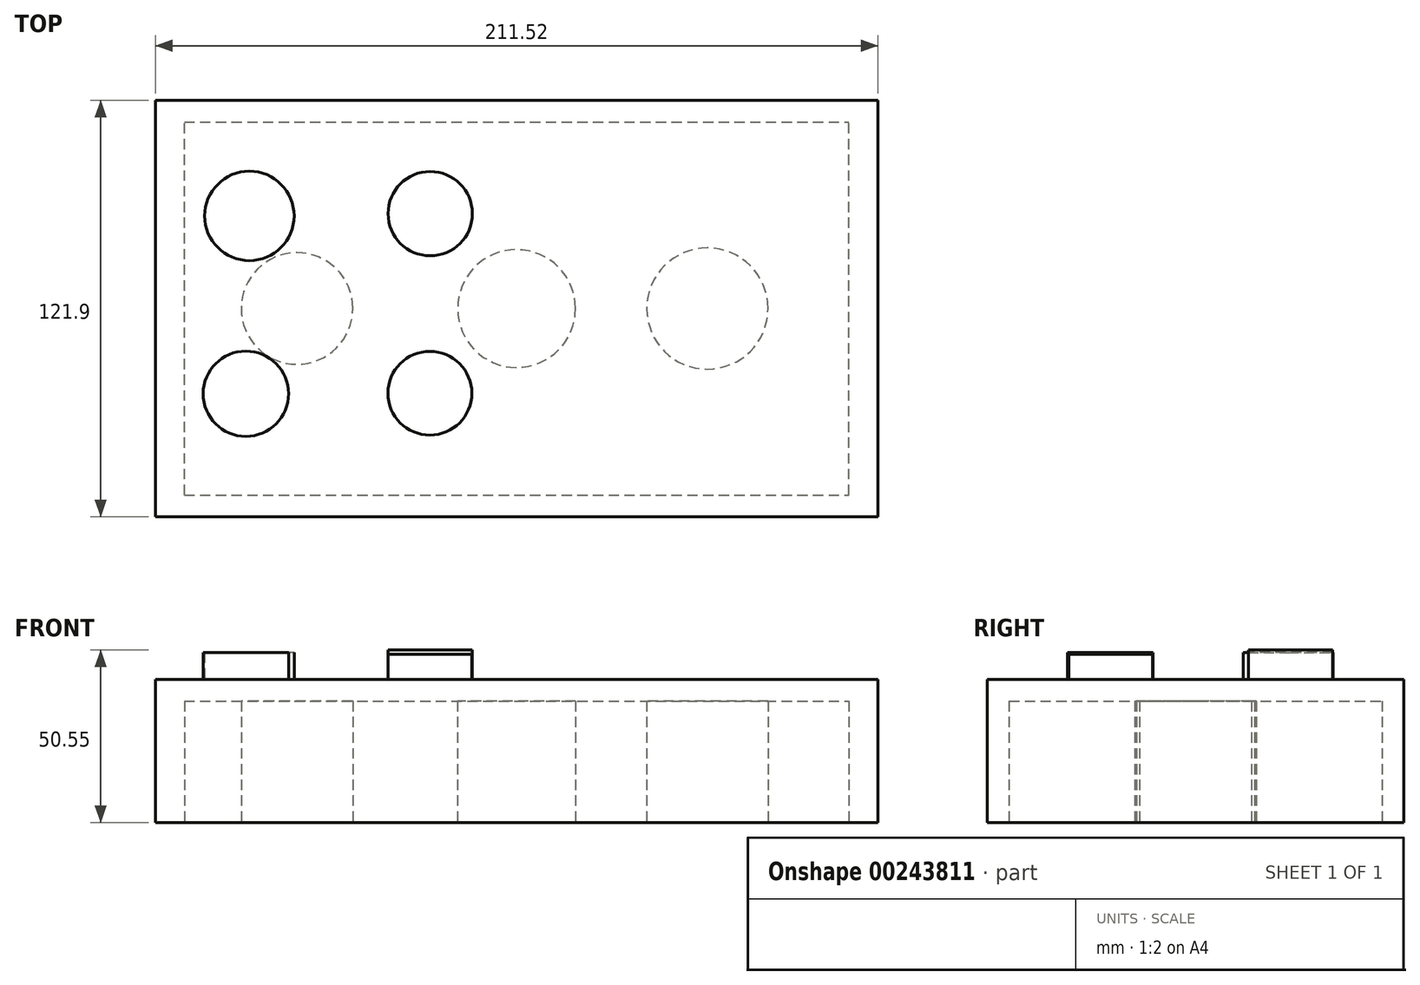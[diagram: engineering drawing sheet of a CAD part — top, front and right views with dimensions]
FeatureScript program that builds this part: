
annotation { "Feature Type Name" : "Feature", "Feature Type Description" : "" }
export const myFeature = defineFeature(function(context is Context, id is Id, definition is map)
    precondition{}
    {
        {
            var Q0;
            Q0=qCreatedBy(makeId("Top.planeOp"),FACE);
            var sketch = newSketch(context, id + "F0", { "sketchPlane" : qUnion([Q0])});
            skLineSegment(sketch, "E0.bottom", {"start": v(-105.76, 60.95) * mm, "end": v(105.76, 60.95) * mm});
            skLineSegment(sketch, "E0.top", {"start": v(-105.76, -60.95) * mm, "end": v(105.76, -60.95) * mm});
            skLineSegment(sketch, "E0.left", {"start": v(-105.76, 60.95) * mm, "end": v(-105.76, -60.95) * mm});
            skLineSegment(sketch, "E0.right", {"start": v(105.76, 60.95) * mm, "end": v(105.76, -60.95) * mm});
            skPoint(sketch, "E0.middle", {"position": v(0, 0) * mm});
            skSolve(sketch);
        }
        {
            var Q0;
            Q0 = qSketchRegion(id + "F0", true);
            extrude(context, id + "F1", {"entities" : qUnion([Q0]), "depth" : 41.9 * mm});
        }
        {
            var Q0;
            Q0=makeQuery(id+"F1.opExtrude","CAP_FACE",FACE,{"disambiguationData":[OSD([sQuery(id+"F0.wireOp",EDGE,"E0.bottom"),sQuery(id+"F0.wireOp",EDGE,"E0.top"),sQuery(id+"F0.wireOp",EDGE,"E0.left"),sQuery(id+"F0.wireOp",EDGE,"E0.right")])],"isStart":false});
            var sketch = newSketch(context, id + "F2", { "sketchPlane" : qUnion([Q0])});
            skCircle(sketch, "E1", {"center": v(-78.22, 27.11) * mm, "radius": 13.1 * mm});
            skSolve(sketch);
        }
        {
            var Q0;
            Q0=makeQuery(id+"F2.imprint","IMPRINT",FACE,{"disambiguationData":[TD([[makeQuery(id+"F2.imprint","IMPRINT",EDGE,{"derivedFrom":sQuery(id+"F2.wireOp",EDGE,"E1")}),1.0]])]});
            extrude(context, id + "F3", {"entities" : qUnion([Q0]), "operationType" : NewBodyOperationType.ADD, "depth" : 7.87 * mm});
        }
        {
            var Q0;
            Q0=makeQuery(id+"F2.imprint","IMPRINT",FACE,{"disambiguationData":[TD([[makeQuery(id+"F2.imprint","IMPRINT",EDGE,{"derivedFrom":sQuery(id+"F2.wireOp",EDGE,"E1")}),-1.0]])]});
            var sketch = newSketch(context, id + "F4", { "sketchPlane" : qUnion([Q0])});
            skCircle(sketch, "E2", {"center": v(-79.26, -24.95) * mm, "radius": 12.5 * mm});
            skSolve(sketch);
        }
        {
            var Q0;
            Q0 = qSketchRegion(id + "F4", true);
            extrude(context, id + "F5", {"entities" : qUnion([Q0]), "operationType" : NewBodyOperationType.ADD, "depth" : 7.87 * mm});
        }
        {
            var Q0;
            Q0=makeQuery(id+"F2.imprint","IMPRINT",FACE,{"disambiguationData":[TD([[makeQuery(id+"F2.imprint","IMPRINT",EDGE,{"derivedFrom":sQuery(id+"F2.wireOp",EDGE,"E1")}),-1.0]])]});
            var sketch = newSketch(context, id + "F6", { "sketchPlane" : qUnion([Q0])});
            skCircle(sketch, "E3", {"center": v(-25.29, 27.78) * mm, "radius": 12.34 * mm});
            skSolve(sketch);
        }
        {
            var Q0;
            Q0 = qSketchRegion(id + "F6", true);
            extrude(context, id + "F7", {"entities" : qUnion([Q0]), "operationType" : NewBodyOperationType.ADD, "depth" : 8.64 * mm});
        }
        {
            var Q0;
            Q0=makeQuery(id+"F2.imprint","IMPRINT",FACE,{"disambiguationData":[TD([[makeQuery(id+"F2.imprint","IMPRINT",EDGE,{"derivedFrom":sQuery(id+"F2.wireOp",EDGE,"E1")}),-1.0]])]});
            var sketch = newSketch(context, id + "F8", { "sketchPlane" : qUnion([Q0])});
            skCircle(sketch, "E4", {"center": v(-25.38, -24.8) * mm, "radius": 12.27 * mm});
            skSolve(sketch);
        }
        {
            var Q0;
            Q0 = qSketchRegion(id + "F8", true);
            extrude(context, id + "F9", {"entities" : qUnion([Q0]), "operationType" : NewBodyOperationType.ADD, "depth" : 7.37 * mm});
        }
        {
            var Q0;
            Q0=makeQuery(id+"F0.imprint","IMPRINT",FACE,{"disambiguationData":[TD([[makeQuery(id+"F0.imprint","IMPRINT",EDGE,{"derivedFrom":sQuery(id+"F0.wireOp",EDGE,"E0.bottom")}),-1.0]])]});
            var sketch = newSketch(context, id + "F10", { "sketchPlane" : qUnion([Q0])});
            skLineSegment(sketch, "E5.bottom", {"start": v(-97.25, -54.56) * mm, "end": v(97.25, -54.56) * mm});
            skLineSegment(sketch, "E5.top", {"start": v(-97.25, 54.56) * mm, "end": v(97.25, 54.56) * mm});
            skLineSegment(sketch, "E5.left", {"start": v(-97.25, -54.56) * mm, "end": v(-97.25, 54.56) * mm});
            skLineSegment(sketch, "E5.right", {"start": v(97.25, -54.56) * mm, "end": v(97.25, 54.56) * mm});
            skPoint(sketch, "E5.middle", {"position": v(0, 0) * mm});
            skSolve(sketch);
        }
        {
            var Q0;
            Q0 = qSketchRegion(id + "F10", true);
            extrude(context, id + "F11", {"entities" : qUnion([Q0]), "operationType" : NewBodyOperationType.REMOVE, "depth" : 35.56 * mm});
        }
        {
            var Q0;
            Q0=makeQuery(id+"F0.imprint","IMPRINT",FACE,{"disambiguationData":[TD([[makeQuery(id+"F0.imprint","IMPRINT",EDGE,{"derivedFrom":sQuery(id+"F0.wireOp",EDGE,"E0.bottom")}),-1.0]])]});
            var sketch = newSketch(context, id + "F12", { "sketchPlane" : qUnion([Q0])});
            skCircle(sketch, "E6", {"center": v(0, 0) * mm, "radius": 17.25 * mm});
            skSolve(sketch);
        }
        {
            var Q0;
            Q0=makeQuery(id+"F12.imprint","IMPRINT",FACE,{"disambiguationData":[TD([[makeQuery(id+"F12.imprint","IMPRINT",EDGE,{"derivedFrom":sQuery(id+"F12.wireOp",EDGE,"E6")}),1.0]])]});
            extrude(context, id + "F13", {"entities" : qUnion([Q0]), "operationType" : NewBodyOperationType.ADD, "depth" : 40.85 * mm});
        }
        {
            var Q0;
            Q0=makeQuery(id+"F0.imprint","IMPRINT",FACE,{"disambiguationData":[TD([[makeQuery(id+"F0.imprint","IMPRINT",EDGE,{"derivedFrom":sQuery(id+"F0.wireOp",EDGE,"E0.bottom")}),-1.0]])]});
            var sketch = newSketch(context, id + "F14", { "sketchPlane" : qUnion([Q0])});
            skCircle(sketch, "E7", {"center": v(-64.27, 0) * mm, "radius": 16.34 * mm});
            skSolve(sketch);
        }
        {
            var Q0;
            Q0=makeQuery(id+"F14.imprint","IMPRINT",FACE,{"disambiguationData":[TD([[makeQuery(id+"F14.imprint","IMPRINT",EDGE,{"derivedFrom":sQuery(id+"F14.wireOp",EDGE,"E7")}),1.0]])]});
            extrude(context, id + "F15", {"entities" : qUnion([Q0]), "operationType" : NewBodyOperationType.ADD, "depth" : 40.94 * mm});
        }
        {
            var Q0;
            Q0=makeQuery(id+"F0.imprint","IMPRINT",FACE,{"disambiguationData":[TD([[makeQuery(id+"F0.imprint","IMPRINT",EDGE,{"derivedFrom":sQuery(id+"F0.wireOp",EDGE,"E0.bottom")}),-1.0]])]});
            var sketch = newSketch(context, id + "F16", { "sketchPlane" : qUnion([Q0])});
            skCircle(sketch, "E8", {"center": v(55.83, 0) * mm, "radius": 17.74 * mm});
            skSolve(sketch);
        }
        {
            var Q0;
            Q0=makeQuery(id+"F16.imprint","IMPRINT",FACE,{"disambiguationData":[TD([[makeQuery(id+"F16.imprint","IMPRINT",EDGE,{"derivedFrom":sQuery(id+"F16.wireOp",EDGE,"E8")}),1.0]])]});
            extrude(context, id + "F17", {"entities" : qUnion([Q0]), "operationType" : NewBodyOperationType.ADD, "depth" : 41.34 * mm});
        }
    });
